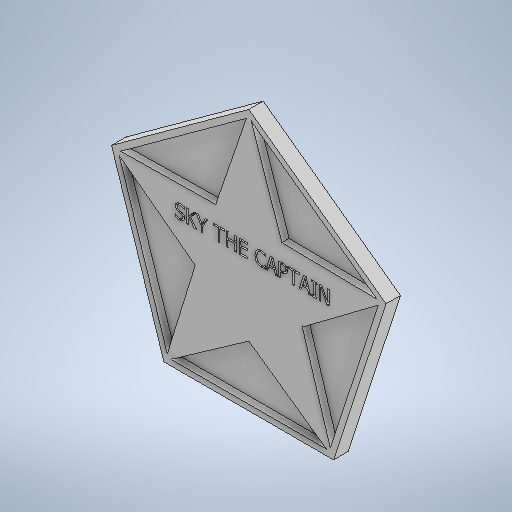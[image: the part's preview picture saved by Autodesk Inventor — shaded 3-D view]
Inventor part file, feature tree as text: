
AUTODESK INVENTOR PART (.ipt)
format: ipt  version: 2025.2 (Build 292293000, 293)  size: 503,808 bytes
history: native  units: in
note: dims shown in document units (in); Inventor stores cm internally (conversion verified against a paired STEP export)
features: sketch x4, extrude x2, emboss x1
ambient origin geometry x8: Origin, YZ Plane, XZ Plane, XY Plane, X Axis, Y Axis, Z Axis, Center Point
bodies: Solid1 (feature_tree)
feature tree (7):
  extrude  "Extrusion1"  Depth=0.1535in
  extrude  "Extrusion2"  Depth=0.0157in
  emboss  "Emboss1"
  sketch  "Sketch1"  dims[d0=0.7874in d1=0.1535in]
  sketch  "Sketch2"  dims[d5=0.0157in]
  sketch  "Sketch Circular Pattern1"  dims[d2=0.0394in d3=0.0in d4=0.0157in]
  sketch  "Sketch3"  dims[d6=0.0157in d7=0.0157in d8=0.0157in d9=0.0079in d10=0.0079in d11=0.0079in d12=0.0079in d13=0.0079in d14=0.0079in d15=0.0079in d16=0.0079in d17=0.0079in d18=0.0079in d19=0.1535in d20=1.9685in d22=360.0deg d24=0.0197in d25=0.0in d26=0.0197in d27=0.0in]
